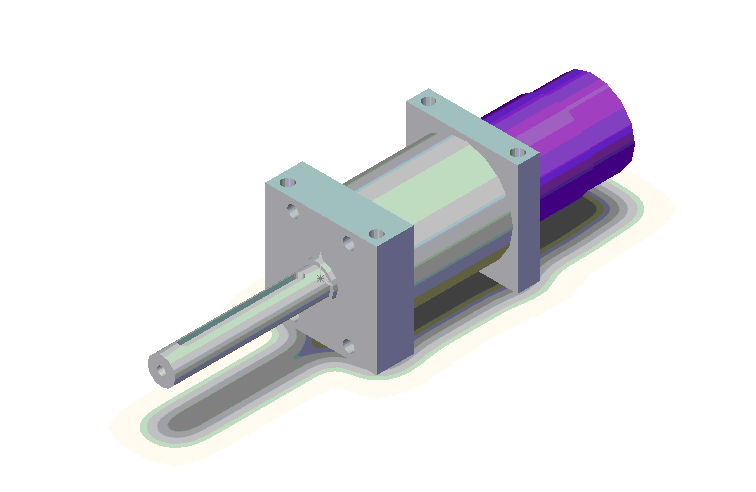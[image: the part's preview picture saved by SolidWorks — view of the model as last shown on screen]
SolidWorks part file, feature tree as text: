
SOLIDWORKS PART (.sldprt)
format: sldprt  version: not decoded by parser v0  size: 542,208 bytes
history: native  units: mm
features: sketch x14, extrude x7, cut_extrude x7, plane x2 (+8 scaffold rows collapsed)
feature tree (38):
  scaffold x8  (default folders/planes/origin — collapsed)
  sketch  "Sketch1"  dims[D13=4.0mm D14=4.0mm D15=4.0mm D16=4.0mm D1=19.05mm D2=38.1mm D3=19.05mm D4=38.1mm D5=9.525mm D6=9.53mm D7=9.53mm D8=9.53mm D9=3.81mm D10=3.81mm D11=34.29mm D12=34.29mm]
  extrude  "Base-Extrude"  Depth=12.7mm
  sketch  "Sketch2"  dims[D1=9.525mm]
  extrude  "Boss-Extrude1"  Depth=54.61mm
  plane  "Plane1"
  sketch  "Sketch3"  dims[D1=3.175mm D2=3.175mm D3=7.62mm D4=39.37mm]
  plane  "Plane2"  Offset=2.7625mm
  cut_extrude  "Cut-Extrude3"  [1 undecoded]
  sketch  "Sketch4"  dims[D1=3.0mm]
  cut_extrude  "Cut-Extrude4"  Depth=9.525mm
  sketch  "Sketch5"
  extrude  "Boss-Extrude2"  Depth=1.5mm
  sketch  "Sketch6"  dims[D1=4.0mm D2=4.0mm D3=3.81mm D4=34.29mm D5=3.81mm D6=3.81mm]
  cut_extrude  "Cut-Extrude5"  Depth=9.5mm
  sketch  "Sketch7"  dims[D1=15.24mm]
  cut_extrude  "Cut-Extrude6"  Depth=9.5mm
  sketch  "Sketch8"  dims[D1=35.0mm]
  extrude  "Boss-Extrude3"  Depth=35.56mm
  sketch  "Sketch9"
  extrude  "Boss-Extrude4"  Depth=7.62mm
  sketch  "Sketch11"  dims[D7=4.0mm D8=4.0mm D9=4.0mm D10=4.0mm D11=4.0mm D12=4.0mm D13=4.0mm D14=4.0mm D1=9.525mm D2=9.525mm D3=28.575mm D4=28.575mm D5=3.81mm D6=34.29mm D15=3.81mm D16=9.53mm D17=28.58mm D18=34.29mm]
  cut_extrude  "Cut-Extrude7"  Depth=9.525mm
  sketch  "Sketch12"  dims[c1.D3=4.0mm c1.D4=4.0mm c1.D1=3.81mm c1.D2=3.81mm c2.D3=3.81mm c2.D5=3.81mm]
  cut_extrude  "Cut-Extrude8"  Depth=9.525mm
  sketch  "Sketch13"
  cut_extrude  "Cut-Extrude9"  Depth=9.525mm
  sketch  "Sketch14"  dims[D1=27.7mm]
  extrude  "Boss-Extrude5"  Depth=37.8mm
  sketch  "Sketch15"  dims[D1=28.956mm]
  extrude  "Boss-Extrude6"  Depth=23mm
decode coverage: 24 of 28 modeling features carry decoded parameters
note: 1 parameter value undecoded
note: suppression state not decoded; provenance and decode notes live in map.json
